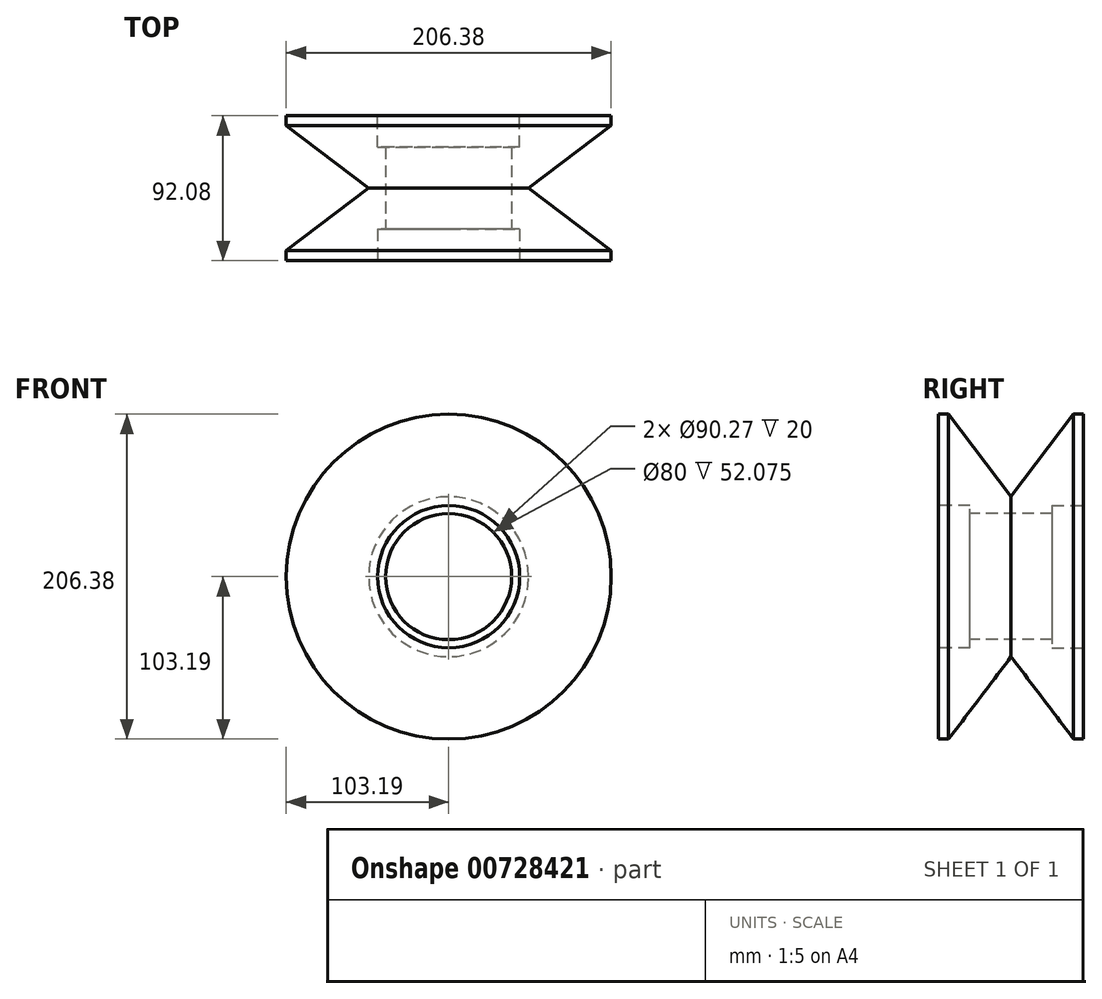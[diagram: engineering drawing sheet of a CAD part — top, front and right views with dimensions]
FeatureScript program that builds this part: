
annotation { "Feature Type Name" : "Feature", "Feature Type Description" : "" }
export const myFeature = defineFeature(function(context is Context, id is Id, definition is map)
    precondition{}
    {
        {
            var Q0;
            Q0=qCreatedBy(makeId("Right.planeOp"),FACE);
            var sketch = newSketch(context, id + "F0", { "sketchPlane" : qUnion([Q0])});
            skPoint(sketch, "E0.middle", {"position": v(0, 0) * mm});
            skLineSegment(sketch, "E1.left", {"start": v(46.04, -103.19) * mm, "end": v(46.04, 103.19) * mm});
            skLineSegment(sketch, "E1.right", {"start": v(-46.04, -103.19) * mm, "end": v(-46.04, 103.19) * mm});
            skLineSegment(sketch, "E2", {"start": v(-46.04, 0) * mm, "end": v(46.04, 0) * mm});
            skLineSegment(sketch, "E3", {"start": v(-46.04, -103.19) * mm, "end": v(-39.69, -103.19) * mm});
            skLineSegment(sketch, "E4", {"start": v(46.04, -103.19) * mm, "end": v(39.69, -103.19) * mm});
            skLineSegment(sketch, "E5", {"start": v(-46.04, 103.19) * mm, "end": v(-39.69, 103.19) * mm});
            skLineSegment(sketch, "E6", {"start": v(46.04, 103.19) * mm, "end": v(39.69, 103.19) * mm});
            skLineSegment(sketch, "E7", {"start": v(39.69, 103.19) * mm, "end": v(0, 50.8) * mm});
            skLineSegment(sketch, "E8", {"start": v(-39.69, 103.19) * mm, "end": v(0, 50.8) * mm});
            skLineSegment(sketch, "E9", {"start": v(0, -50.8) * mm, "end": v(39.69, -103.19) * mm});
            skLineSegment(sketch, "E10", {"start": v(0, -50.8) * mm, "end": v(-39.69, -103.19) * mm});
            skLineSegment(sketch, "E11", {"start": v(0, 50.8) * mm, "end": v(0, -50.8) * mm});
            skSolve(sketch);
        }
        {
            var Q0;
            {var subQ1=sQuery(id+"F0.wireOp",EDGE,"E2");Q0=makeQuery(id+"F0.imprint","IMPRINT",FACE,{"disambiguationData":[TD([[makeQuery(id+"F0.imprint","IMPRINT",EDGE,{"derivedFrom":subQ1}),1.0]])]});}
            var Q1;
            Q1=sQuery(id+"F0.wireOp",EDGE,"E2");
            revolve(context, id + "F1", {"surfaceOperationType" : NewSurfaceOperationType.NEW, "entities" : qUnion([Q0]), "axis" : qUnion([Q1]), "revolveType" : RevolveType.FULL});
        }
        {
            var Q0;
            Q0=makeQuery(id+"F1.opRevolve","SWEPT_FACE",FACE,{"disambiguationData":[OSD([sQuery(id+"F0.wireOp",EDGE,"E1.left")])]});
            var sketch = newSketch(context, id + "F2", { "sketchPlane" : qUnion([Q0])});
            skCircle(sketch, "E12", {"center": v(0, 0) * mm, "radius": 45.14 * mm});
            skSolve(sketch);
        }
        {
            var Q0;
            Q0=makeQuery(id+"F2.imprint","IMPRINT",FACE,{"disambiguationData":[TD([[makeQuery(id+"F2.imprint","IMPRINT",EDGE,{"derivedFrom":sQuery(id+"F2.wireOp",EDGE,"E12")}),1.0]])]});
            extrude(context, id + "F3", {"entities" : qUnion([Q0]), "operationType" : NewBodyOperationType.REMOVE, "oppositeDirection" : true, "depth" : 20 * mm, "offsetDistance" : 25.4 * mm});
        }
        {
            var Q0;
            Q0=makeQuery(id+"F1.opRevolve","SWEPT_FACE",FACE,{"disambiguationData":[OSD([sQuery(id+"F0.wireOp",EDGE,"E1.right")])]});
            var sketch = newSketch(context, id + "F4", { "sketchPlane" : qUnion([Q0])});
            skCircle(sketch, "E13", {"center": v(0, 0) * mm, "radius": 45.14 * mm});
            skSolve(sketch);
        }
        {
            var Q0;
            Q0 = qSketchRegion(id + "F4", true);
            extrude(context, id + "F5", {"entities" : qUnion([Q0]), "operationType" : NewBodyOperationType.REMOVE, "oppositeDirection" : true, "depth" : 20 * mm, "offsetDistance" : 25.4 * mm});
        }
        {
            var Q0;
            Q0=makeQuery(id+"F5.boolean.opBoolean","COPY",FACE,{"derivedFrom":makeQuery(id+"F5.opExtrude","CAP_FACE",FACE,{"disambiguationData":[OSD([sQuery(id+"F4.wireOp",EDGE,"E13")])],"isStart":false})});
            var sketch = newSketch(context, id + "F6", { "sketchPlane" : qUnion([Q0])});
            skCircle(sketch, "E14", {"center": v(0, 0) * mm, "radius": 40 * mm});
            skSolve(sketch);
        }
        {
            var Q0;
            Q0 = qSketchRegion(id + "F6", true);
            extrude(context, id + "F7", {"entities" : qUnion([Q0]), "operationType" : NewBodyOperationType.REMOVE, "oppositeDirection" : true, "depth" : 127 * mm, "offsetDistance" : 25.4 * mm});
        }
    });
